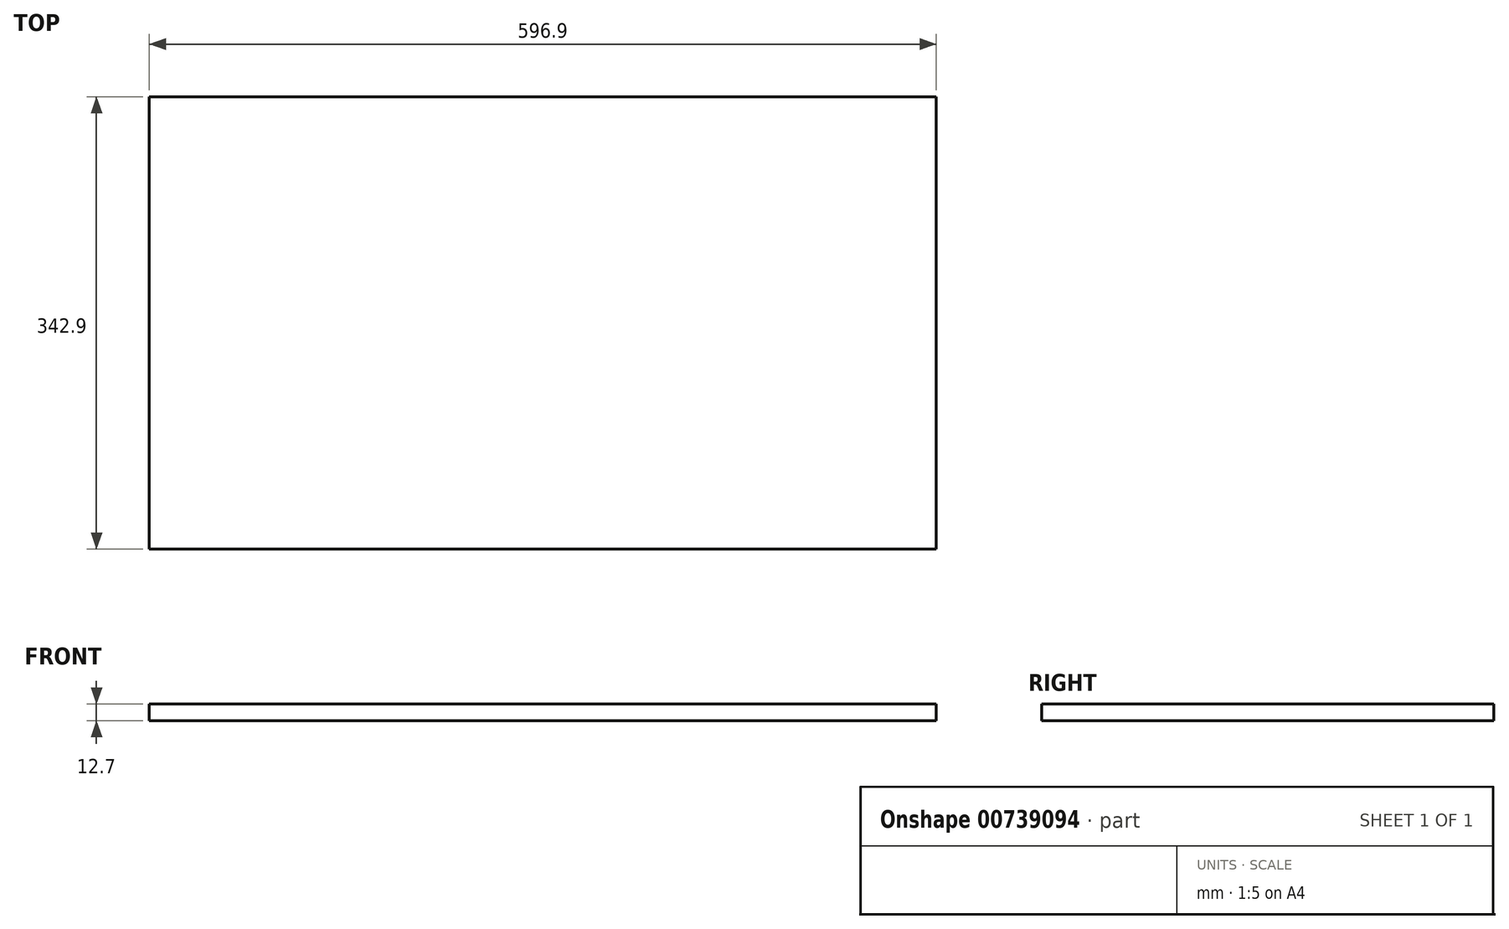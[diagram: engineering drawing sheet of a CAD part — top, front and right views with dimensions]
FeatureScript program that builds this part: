
annotation { "Feature Type Name" : "Feature", "Feature Type Description" : "" }
export const myFeature = defineFeature(function(context is Context, id is Id, definition is map)
    precondition{}
    {
        {
            var Q0;
            Q0=qCreatedBy(makeId("Top.planeOp"),FACE);
            var sketch = newSketch(context, id + "F0", { "sketchPlane" : qUnion([Q0])});
            skLineSegment(sketch, "E0.bottom", {"start": v(0, 0) * mm, "end": v(596.9, 0) * mm});
            skLineSegment(sketch, "E0.top", {"start": v(0, 342.9) * mm, "end": v(596.9, 342.9) * mm});
            skLineSegment(sketch, "E0.left", {"start": v(0, 0) * mm, "end": v(0, 342.9) * mm});
            skLineSegment(sketch, "E0.right", {"start": v(596.9, 0) * mm, "end": v(596.9, 342.9) * mm});
            skSolve(sketch);
        }
        {
            var Q0;
            Q0=makeQuery(id+"F0.imprint","IMPRINT",FACE,{"disambiguationData":[TD([[makeQuery(id+"F0.imprint","IMPRINT",EDGE,{"derivedFrom":sQuery(id+"F0.wireOp",EDGE,"E0.bottom")}),1.0]])]});
            extrude(context, id + "F1", {"entities" : qUnion([Q0]), "depth" : 12.7 * mm, "offsetDistance" : 25.4 * mm});
        }
    });
